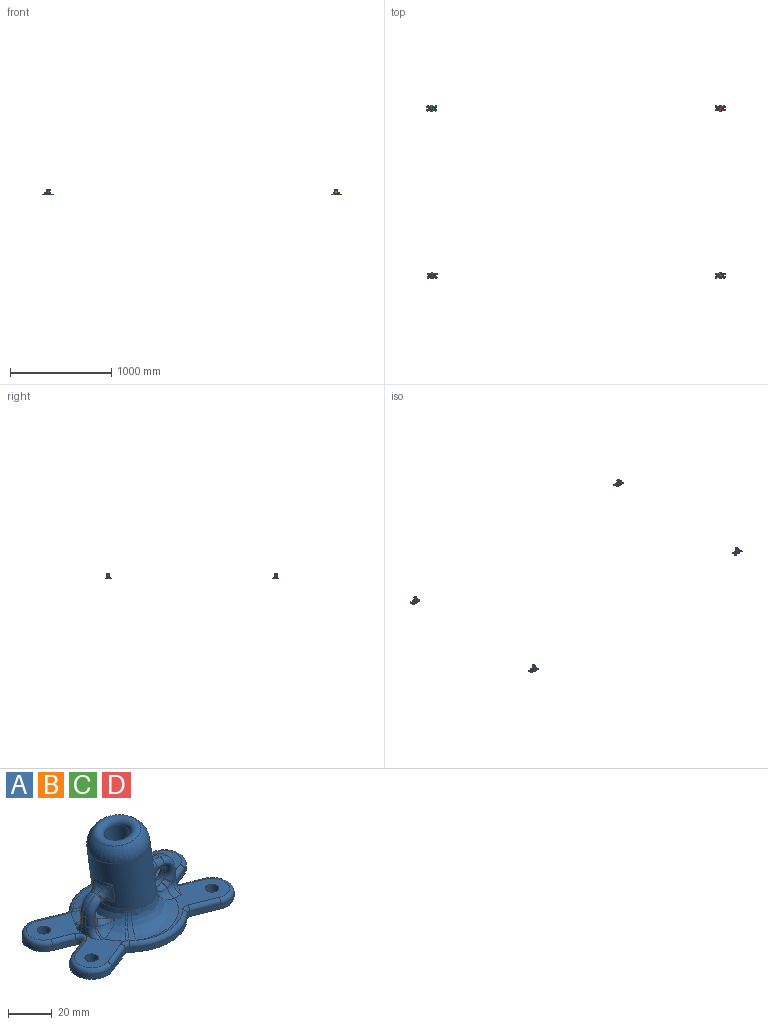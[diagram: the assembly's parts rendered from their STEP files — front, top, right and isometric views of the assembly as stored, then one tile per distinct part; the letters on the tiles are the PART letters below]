
ASSEMBLY  parts=4 mates=1
PART A: 127 faces, bbox 103x62x58.7 mm
  f0: plane 0.92x0.51mm, normal (0,-1,0), area 0.2mm2, adj f74,f121,f122
  f1: plane 1.24x0.85mm, normal (0,1,0), area 0.5mm2, adj f81,f114,f115
  f2: plane 29.24x24.36mm, normal (0,0,1), area 316.6mm2, adj f28,f32,f33,f34,f36,f38,f58,f70
  f3: plane 46.52x25.9mm, normal (0,0,1), area 344.7mm2, adj f4,f30,f43,f45,f47,f49,f50,f51
  f4: bspline ~21.52x19.35mm, area 294.6mm2, adj f3,f53,f59,f79,f80
  f5: plane 62.69x25.94mm, normal (0,0,1), area 378.2mm2, adj f29,f40,f42,f44,f46,f48,f50,f57
  f6: cylinder r=2mm len=2.88mm, axis (0,0,-1), area 6.6mm2, adj f7,f25,f27,f42
  f7: plane 14.39x5.72mm, normal (-0.37,-0.93,0), area 44.5mm2, adj f6,f8,f27,f44
  f8: cylinder r=10mm len=19.29mm, axis (0,0,-1), area 90.3mm2, adj f7,f9,f27,f46
  f9: plane 10.94x4.35mm, normal (0.37,0.93,0), area 33.8mm2, adj f8,f10,f27,f48
  f10: cylinder r=2mm len=3.72mm, axis (0,0,-1), area 13.7mm2, adj f9,f11,f27,f50
  f11: plane 10.94x4.35mm, normal (0.37,-0.93,0), area 33.8mm2, adj f10,f12,f27,f51
  f12: cylinder r=10mm len=19.29mm, axis (0,0,-1), area 90.3mm2, adj f11,f13,f27,f49
  f13: plane 14.39x5.72mm, normal (-0.37,0.93,0), area 44.5mm2, adj f12,f14,f27,f47
  f14: cylinder r=2mm len=2.88mm, axis (0,0,-1), area 6.6mm2, adj f13,f15,f27,f45
  f15: cylinder r=27.08mm len=37.58mm, axis (0,0,-1), area 119.4mm2, adj f14,f16,f27,f43
  f16: cylinder r=2mm len=2.88mm, axis (0,0,-1), area 6.6mm2, adj f15,f17,f27,f41
  f17: plane 14.39x5.72mm, normal (0.37,0.93,0), area 44.5mm2, adj f16,f18,f27,f39
  f18: cylinder r=10mm len=19.29mm, axis (0,0,-1), area 90.3mm2, adj f17,f19,f27,f37
  f19: plane 10.94x4.35mm, normal (-0.37,-0.93,0), area 33.8mm2, adj f18,f20,f27,f35
  f20: cylinder r=2mm len=3.72mm, axis (0,0,-1), area 13.7mm2, adj f19,f21,f27,f33
  f21: plane 10.94x4.35mm, normal (-0.37,0.93,0), area 33.8mm2, adj f20,f22,f27,f32
  f22: cylinder r=10mm len=19.29mm, axis (0,0,-1), area 90.3mm2, adj f21,f23,f27,f34
  f23: plane 14.39x5.72mm, normal (0.37,-0.93,0), area 44.5mm2, adj f22,f24,f27,f36
  f24: cylinder r=2mm len=2.88mm, axis (0,0,-1), area 6.6mm2, adj f23,f25,f27,f38
  f25: cylinder r=27.08mm len=37.58mm, axis (0,0,-1), area 119.4mm2, adj f6,f24,f27,f40
  f26: plane 27.83x24.36mm, normal (0,0,1), area 310.7mm2, adj f31,f33,f35,f37,f39,f41,f58,f70
  f27: plane 98x54.15mm, normal (0,0,-1), area 4064.1mm2, adj f6,f7,f8,f9,f10,f11,f12,f13
  f28: cylinder r=3.1mm len=6.2mm, axis (0,0,-1), area 97.4mm2, adj f2,f27
  f29: cylinder r=3.1mm len=6.2mm, axis (0,0,-1), area 97.4mm2, adj f5,f27
  f30: cylinder r=3.1mm len=6.2mm, axis (0,0,-1), area 97.4mm2, adj f3,f27
  f31: cylinder r=3.1mm len=6.2mm, axis (0,0,-1), area 97.4mm2, adj f26,f27
  f32: cylinder r=2.12mm len=11.73mm, axis (0.93,0.37,0), area 39.3mm2, adj f2,f21,f33,f34
  f33: torus R=4.12mm, axis (0,0,1), area 22.1mm2, adj f2,f20,f26,f32,f35
  f34: torus R=7.88mm, axis (0,0,1), area 96.8mm2, adj f2,f22,f32,f36
  f35: cylinder r=2.12mm len=11.73mm, axis (-0.93,0.37,0), area 39.3mm2, adj f19,f26,f33,f37
  f36: cylinder r=2.12mm len=15.17mm, axis (-0.93,-0.37,0), area 51.7mm2, adj f2,f23,f34,f38
  f37: torus R=7.88mm, axis (0,0,1), area 96.8mm2, adj f18,f26,f35,f39
  f38: torus R=4.12mm, axis (0,0,1), area 10.6mm2, adj f2,f24,f36,f40,f56
  f39: cylinder r=2.12mm len=15.17mm, axis (0.93,-0.37,0), area 51.7mm2, adj f17,f26,f37,f41
  f40: torus R=24.95mm, axis (0,0,1), area 134.6mm2, adj f5,f25,f38,f42,f55
  f41: torus R=4.12mm, axis (0,0,1), area 10.2mm2, adj f16,f26,f39,f43,f60
  f42: torus R=4.12mm, axis (0,0,1), area 10.6mm2, adj f5,f6,f40,f44
  f43: torus R=24.95mm, axis (0,0,1), area 132.7mm2, adj f3,f15,f41,f45,f59
  f44: cylinder r=2.12mm len=15.17mm, axis (-0.93,0.37,0), area 51.7mm2, adj f5,f7,f42,f46
  f45: torus R=4.12mm, axis (0,0,1), area 10.6mm2, adj f3,f14,f43,f47
  f46: torus R=7.88mm, axis (0,0,1), area 96.8mm2, adj f5,f8,f44,f48
  f47: cylinder r=2.12mm len=15.17mm, axis (0.93,0.37,0), area 51.7mm2, adj f3,f13,f45,f49
  f48: cylinder r=2.12mm len=11.73mm, axis (0.93,-0.37,0), area 39.3mm2, adj f5,f9,f46,f50
  f49: torus R=7.88mm, axis (0,0,1), area 96.8mm2, adj f3,f12,f47,f51
  f50: torus R=4.12mm, axis (0,0,1), area 22.1mm2, adj f3,f5,f10,f48,f51
  f51: cylinder r=2.12mm len=11.73mm, axis (-0.93,-0.37,0), area 39.3mm2, adj f3,f11,f49,f50
  f52: cylinder r=6mm len=47.52mm, axis (0.14,0,-0.99), area 1745.6mm2, adj f54,f126
  f53: cylinder r=14.5mm len=36.92mm, axis (0.14,0,-0.99), area 2429.6mm2, adj f4,f55,f56,f57,f58,f59,f60,f61
  f54: plane 15.49x15.37mm, normal (0,0,1), area 114.2mm2, adj f52
  f55: bspline ~12.8x11.19mm, area 39.4mm2, adj f40,f53,f56,f57
  f56: bspline ~11.22x9.55mm, area 18.6mm2, adj f38,f53,f55,f58
  f57: bspline ~36.1x18.83mm, area 478mm2, adj f5,f53,f55,f75
  f58: bspline ~33.93x14.48mm, area 286.6mm2, adj f2,f26,f53,f56,f60,f71,f82,f88
  f59: bspline ~23.43x15.47mm, area 240.1mm2, adj f4,f43,f53,f60
  f60: bspline ~11.28x9.7mm, area 32.4mm2, adj f41,f53,f58,f59
  f61: torus R=4.5mm, axis (-0.14,0,0.99), area 728mm2, adj f53,f126
  f62: plane 8.44x3.95mm, normal (0.14,0,0.99), area 18.8mm2, adj f53,f66,f107,f110,f118,f121
  f63: plane 9.61x3.23mm, normal (-1,0,0), area 4.3mm2, adj f53,f74,f118
  f64: plane 10.11x5.51mm, normal (1,0,0), area 25.8mm2, adj f3,f5,f66,f115,f116,f124,f125
  f65: cylinder r=5mm len=10mm, axis (0,1,0), area 98.8mm2, adj f106,f108,f109,f111,f112,f114,f117,f119
  f66: cylinder r=10mm len=9.91mm, axis (0,1,0), area 28.7mm2, adj f62,f64,f113,f123
  f67: plane 1.24x0.85mm, normal (0,-1,0), area 0.5mm2, adj f76,f122,f124
  f68: plane 0.3x0.15mm, normal (0,1,0), area 0mm2, adj f77,f110,f114
  f69: cylinder r=10mm len=9.48mm, axis (0,1,0), area 24.9mm2, adj f70,f86,f94,f102
  f70: plane 10.11x5.51mm, normal (-1,0,0), area 25.8mm2, adj f2,f26,f69,f95,f96,f104,f105
  f71: cylinder r=5mm len=10mm, axis (0,1,0), area 48.1mm2, adj f53,f58,f89,f90,f93,f97,f100,f101
  f72: plane 1.24x0.85mm, normal (0,-1,0), area 0.5mm2, adj f83,f103,f104
  f73: plane 1.24x0.84mm, normal (0,1,0), area 0.5mm2, adj f87,f88,f93,f95
  f74: cylinder r=5mm len=10.42mm, axis (0.14,0,-0.99), area 22.6mm2, adj f0,f53,f63,f75,f118,f120
  f75: bspline ~11.14x10.94mm, area 48.4mm2, adj f57,f74,f76,f117
  f76: cylinder r=5mm len=5mm, axis (-1,0,0), area 29.7mm2, adj f5,f67,f75,f119,f125
  f77: cylinder r=5mm len=5.97mm, axis (0.14,0,-0.99), area 19.4mm2, adj f53,f68,f78,f107,f111
  f78: bspline ~6.97x4.82mm, area 10.4mm2, adj f53,f77,f79,f108
  f79: bspline ~8.67x7.99mm, area 28.7mm2, adj f4,f78,f80,f106
  f80: bspline ~7.11x5.76mm, area 18.6mm2, adj f4,f79,f81,f109
  f81: cylinder r=5mm len=5mm, axis (1,0,0), area 26.6mm2, adj f1,f3,f80,f112,f116
  f82: bspline ~10.31x8.11mm, area 34mm2, adj f58,f83,f97
  f83: cylinder r=5mm len=5mm, axis (1,0,0), area 8.5mm2, adj f2,f72,f82,f101,f105
  f84: cylinder r=5mm len=10.92mm, axis (0.14,0,-0.99), area 22.3mm2, adj f53,f99,f100
  f85: cylinder r=5mm len=10.38mm, axis (0.14,0,-0.99), area 21.1mm2, adj f53,f90,f91
  f86: bspline ~21.1x6.35mm, area 41.3mm2, adj f53,f69,f91,f92,f98,f99
  f87: cylinder r=5mm len=5mm, axis (-1,0,0), area 4.9mm2, adj f26,f73,f88,f96
  f88: bspline ~10.4x8.08mm, area 39.7mm2, adj f58,f73,f87,f89
  f89: bspline ~9.93x6.34mm, area 26.1mm2, adj f58,f71,f88,f93
  f90: bspline ~6.6x6.38mm, area 17.8mm2, adj f53,f71,f85,f91,f93
  f91: bspline ~8.89x5.84mm, area 22.7mm2, adj f85,f86,f90,f92,f93
  f92: bspline ~3.21x3.01mm, area 1.3mm2, adj f86,f91,f93,f94
  f93: torus R=8mm, axis (0,-1,0), area 51.2mm2, adj f71,f73,f89,f90,f91,f92,f94,f95
  f94: torus R=7mm, axis (0,-1,0), area 47.6mm2, adj f69,f92,f93,f95
  f95: cylinder r=3mm len=5.11mm, axis (0,0,-1), area 23.1mm2, adj f70,f73,f93,f94,f96
  f96: torus R=8mm, axis (1,0,0), area 31.1mm2, adj f26,f70,f87,f95
  f97: bspline ~10.08x6.2mm, area 26.1mm2, adj f58,f71,f82,f101
  f98: bspline ~3.67x3.43mm, area 3.2mm2, adj f86,f99,f102,f103
  f99: bspline ~8.81x5.52mm, area 21.6mm2, adj f84,f86,f98,f100,f103
  f100: bspline ~6.31x6.03mm, area 17.1mm2, adj f53,f71,f84,f99,f103
  f101: bspline ~3.21x3.14mm, area 1.1mm2, adj f71,f83,f97,f103
  f102: torus R=7mm, axis (0,-1,0), area 47.8mm2, adj f69,f98,f103,f104
  f103: torus R=8mm, axis (0,-1,0), area 53.1mm2, adj f71,f72,f98,f99,f100,f101,f102,f104
  f104: cylinder r=3mm len=5.11mm, axis (0,0,1), area 23.1mm2, adj f70,f72,f102,f103,f105
  f105: torus R=8mm, axis (1,0,0), area 31.1mm2, adj f2,f70,f83,f104
  f106: bspline ~6.82x5.85mm, area 18.7mm2, adj f65,f79,f108,f109
  f107: bspline ~7.43x5.84mm, area 22.7mm2, adj f53,f62,f77,f110
  f108: bspline ~6.47x2.56mm, area 10.5mm2, adj f65,f78,f106,f111
  f109: bspline ~4.01x3.3mm, area 8.2mm2, adj f65,f80,f106,f112
  f110: cylinder r=3mm len=4.55mm, axis (-0.99,0,0.14), area 18.7mm2, adj f62,f68,f107,f113,f114
  f111: bspline ~6.41x4.61mm, area 15mm2, adj f65,f77,f108,f114
  f112: bspline ~5.09x4.08mm, area 10.5mm2, adj f65,f81,f109,f114
  f113: torus R=7mm, axis (0,-1,0), area 54.9mm2, adj f66,f110,f114,f115
  f114: torus R=8mm, axis (0,-1,0), area 69mm2, adj f1,f65,f68,f110,f111,f112,f113,f115
  f115: cylinder r=3mm len=5.11mm, axis (0,0,1), area 23.1mm2, adj f1,f64,f113,f114,f116
  f116: torus R=8mm, axis (1,0,0), area 31.1mm2, adj f3,f64,f81,f115
  f117: bspline ~9.86x6.14mm, area 30.5mm2, adj f65,f75,f119,f120
  f118: bspline ~5.49x4.27mm, area 17.9mm2, adj f53,f62,f63,f74,f121
  f119: bspline ~6.16x4.38mm, area 12mm2, adj f65,f76,f117,f122
  f120: bspline ~10.31x4.53mm, area 25.3mm2, adj f65,f74,f117,f122
  f121: cylinder r=3mm len=5.17mm, axis (0.99,0,-0.14), area 21.6mm2, adj f0,f62,f118,f122,f123
  f122: torus R=8mm, axis (0,-1,0), area 71.3mm2, adj f0,f65,f67,f119,f120,f121,f123,f124
  f123: torus R=7mm, axis (0,-1,0), area 54.9mm2, adj f66,f121,f122,f124
  f124: cylinder r=3mm len=5.11mm, axis (0,0,-1), area 23.1mm2, adj f64,f67,f122,f123,f125
  f125: torus R=8mm, axis (1,0,0), area 31.1mm2, adj f5,f64,f76,f124
  f126: torus R=9mm, axis (-0.14,0,0.99), area 341.6mm2, adj f52,f61
PART B: same geometry as A
PART C: same geometry as A
PART D: same geometry as A
PLACE A rot(axis=(0,0,-1),180deg) t=(-2805.8,-1635.5,0)mm
PLACE B t=(-39,-1666.5,0)mm
PLACE C rot(axis=(0,0,-1),180deg) t=(-2808.42,15.13,0)mm
PLACE D t=(-39,-15.5,0)mm
MATE fastened B.f15 <-> D.f27  axis (0,0,-1) through (0,-1651,0)mm
